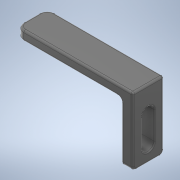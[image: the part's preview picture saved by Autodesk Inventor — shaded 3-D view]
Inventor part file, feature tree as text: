
AUTODESK INVENTOR PART (.ipt)
format: ipt  version: 2020 (Build 240168000, 168)  size: 324,608 bytes
history: native  units: mm
features: fillet x12, extrude x4, sketch x4, projected_geometry x2, hole x1
ambient origin geometry x8: Origin, YZ Plane, XZ Plane, XY Plane, X Axis, Y Axis, Z Axis, Center Point
bodies: Solid1 (feature_tree)
feature tree (23):
  extrude  "Extrusion1"  Depth=8.0mm
  extrude  "Extrusion2"  Depth=3.0mm
  extrude  "Extrusion3"  Depth=4.0mm
  extrude  "Extrusion5"  Depth=0.25mm
  hole  "Hole1"  [1 undecoded]
  fillet  "Fillet10"  Radius=30.0mm
  fillet  "Fillet11"  Radius=2.5mm
  fillet  "Fillet12"  Radius=1.0mm
  fillet  "Fillet15"  Radius=1.0mm
  fillet  "Fillet13"  Radius=1.0mm
  fillet  "Fillet5"  Radius=0.5mm
  fillet  "Fillet16"  Radius=0.25mm
  fillet  "Fillet7"  Radius=6.0mm
  fillet  "Fillet6"  Radius=12.0mm
  fillet  "Fillet14"  [1 undecoded]
  fillet  "Fillet8"  Radius=1.0mm
  fillet  "Fillet9"  Radius=2.0mm
  sketch  "Sketch1"  dims[d0=3.0mm d1=8.0mm]
  sketch  "Sketch2"  dims[d2=1.0mm d3=3.0mm]
  sketch  "Sketch3"  dims[d4=15.0mm d5=0.0mm d6=4.0mm]
  projected_geometry  "Projected Loop1"
  sketch  "Sketch5"  dims[d7=3.2mm d8=4.0mm d9=0.0mm d10=0.0mm d11=30.0mm d13=2.5mm d14=0.0mm d25=1.0mm d26=1.0mm d27=1.0mm d28=0.5mm d29=0.25mm d30=6.0mm d31=12.0mm d32=30.0deg d33=1.0mm d34=2.0mm d35=0.0mm d37=3.5mm d38=6.0mm d39=4.0mm d40=2.0mm d41=90.0deg d42=8.0mm d43=20.594885mm d44=0.5mm d45=2.0mm d46=1.0mm d47=2.0mm d48=2.0mm d49=0.5mm d50=1.0mm d51=2.0mm d52=4.0mm d53=7.0mm d12=0.375mm d15=20.594885mm d16=0.0625mm d17=0.75mm d18=0.375mm d54=0.75mm d55=0.375mm]
  projected_geometry  "Projected Loop3"
note: 2 required parameter values undecoded (feature->parameter linkage not recoverable at this tier; creation-order binding heuristic only, values carry confidence <= 0.55)
